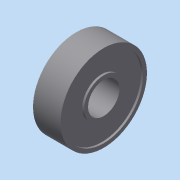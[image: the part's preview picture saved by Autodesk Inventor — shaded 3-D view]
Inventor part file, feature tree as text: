
AUTODESK INVENTOR PART (.ipt)
format: ipt  version: 2014 SP1 (Build 180222100, 222)  size: 111,104 bytes
history: native  units: in
note: dims shown in document units (in); Inventor stores cm internally (conversion verified against a paired STEP export)
features: extrude x2, sketch x2, plane x1, mirror x1, projected_geometry x1
ambient origin geometry x8: Origin, YZ Plane, XZ Plane, XY Plane, X Axis, Y Axis, Z Axis, Center Point
bodies: Solid1 (feature_tree)
feature tree (7):
  extrude  "Extrusion1"  Depth=0.8661in
  plane  "Work Plane1"
  extrude  "Extrusion2"  Depth=0.0197in
  mirror  "Mirror1"
  sketch  "Sketch1"  dims[d0=0.315in d1=0.8661in]
  sketch  "Sketch2"  dims[d2=0.2756in d3=0.0in d4=0.0394in d5=0.0394in d6=0.0197in d7=0.0in]
  projected_geometry  "Projected Loop1"
